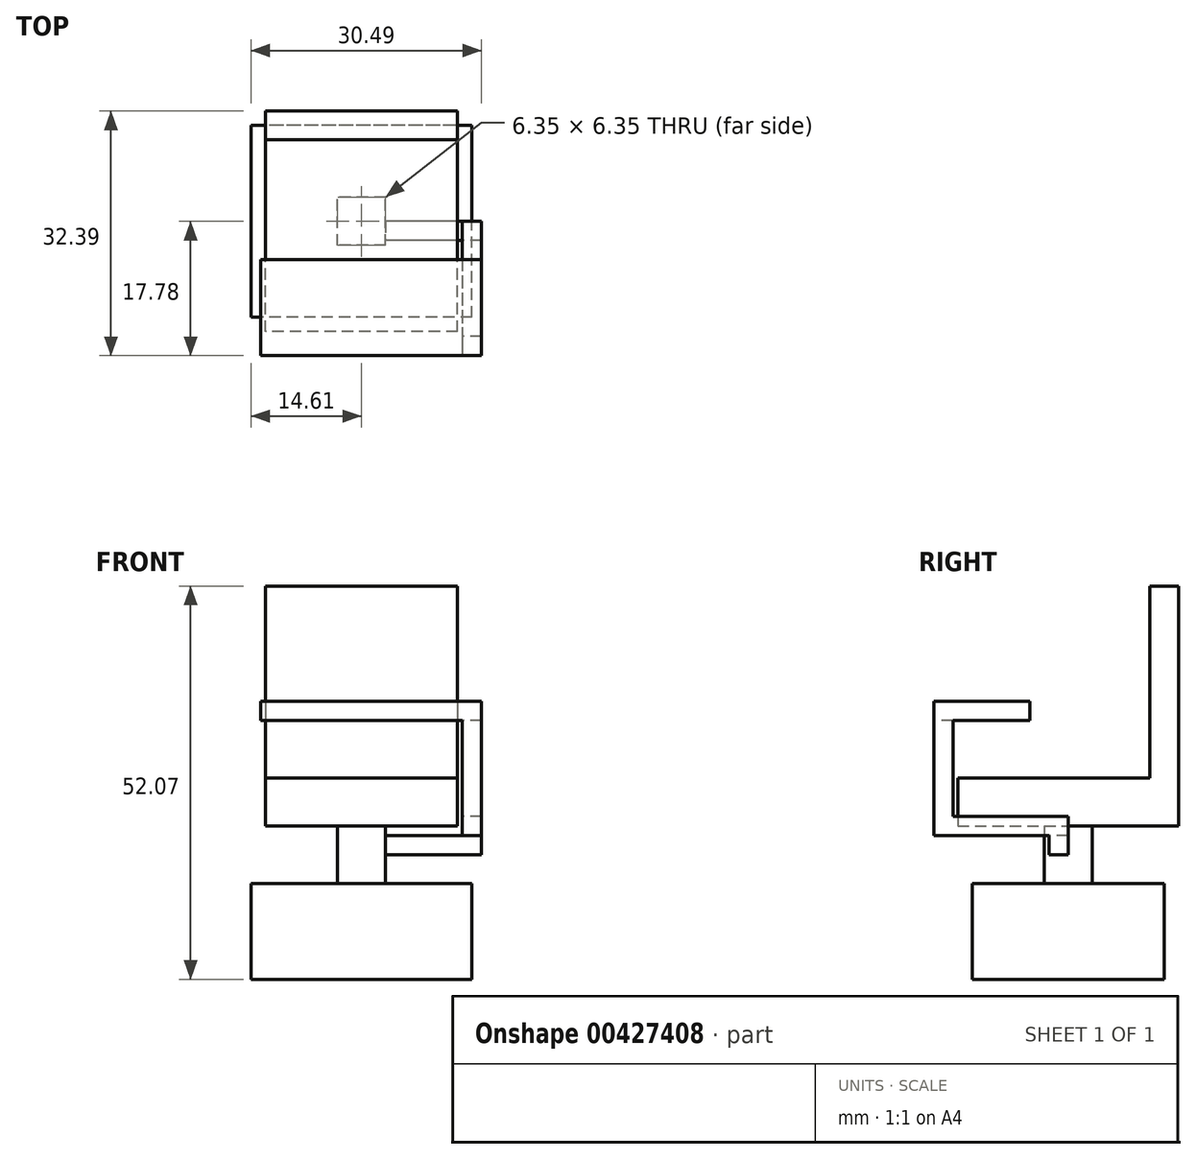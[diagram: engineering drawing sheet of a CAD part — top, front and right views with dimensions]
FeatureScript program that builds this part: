
annotation { "Feature Type Name" : "Feature", "Feature Type Description" : "" }
export const myFeature = defineFeature(function(context is Context, id is Id, definition is map)
    precondition{}
    {
        {
            var Q0;
            Q0=qCreatedBy(makeId("Top.planeOp"),FACE);
            var sketch = newSketch(context, id + "F0", { "sketchPlane" : qUnion([Q0])});
            skLineSegment(sketch, "E0.bottom", {"start": v(14.6, -12.7) * mm, "end": v(-14.6, -12.7) * mm});
            skLineSegment(sketch, "E0.top", {"start": v(14.6, 12.7) * mm, "end": v(-14.6, 12.7) * mm});
            skLineSegment(sketch, "E0.left", {"start": v(14.6, -12.7) * mm, "end": v(14.6, 12.7) * mm});
            skLineSegment(sketch, "E0.right", {"start": v(-14.6, -12.7) * mm, "end": v(-14.6, 12.7) * mm});
            skPoint(sketch, "E0.middle", {"position": v(0, 0) * mm});
            skSolve(sketch);
        }
        {
            var Q0;
            Q0 = qSketchRegion(id + "F0", true);
            extrude(context, id + "F1", {"entities" : qUnion([Q0]), "depth" : 12.7 * mm});
        }
        {
            var Q0;
            Q0=makeQuery(id+"F1.opExtrude","CAP_FACE",FACE,{"disambiguationData":[OSD([sQuery(id+"F0.wireOp",EDGE,"E0.bottom"),sQuery(id+"F0.wireOp",EDGE,"E0.top"),sQuery(id+"F0.wireOp",EDGE,"E0.left"),sQuery(id+"F0.wireOp",EDGE,"E0.right")])],"isStart":false});
            var sketch = newSketch(context, id + "F2", { "sketchPlane" : qUnion([Q0])});
            skLineSegment(sketch, "E1.bottom", {"start": v(3.18, -3.18) * mm, "end": v(-3.18, -3.18) * mm});
            skLineSegment(sketch, "E1.top", {"start": v(3.18, 3.18) * mm, "end": v(-3.18, 3.18) * mm});
            skLineSegment(sketch, "E1.left", {"start": v(3.18, -3.18) * mm, "end": v(3.18, 3.17) * mm});
            skLineSegment(sketch, "E1.right", {"start": v(-3.18, -3.18) * mm, "end": v(-3.18, 3.17) * mm});
            skPoint(sketch, "E1.middle", {"position": v(0, 0) * mm});
            skSolve(sketch);
        }
        {
            var Q0;
            Q0 = qSketchRegion(id + "F2", true);
            extrude(context, id + "F3", {"entities" : qUnion([Q0]), "operationType" : NewBodyOperationType.ADD, "depth" : 7.62 * mm});
        }
        {
            var Q0;
            Q0=makeQuery(id+"F3.opExtrude","CAP_FACE",FACE,{"disambiguationData":[OSD([sQuery(id+"F2.wireOp",EDGE,"E1.bottom"),sQuery(id+"F2.wireOp",EDGE,"E1.top"),sQuery(id+"F2.wireOp",EDGE,"E1.left"),sQuery(id+"F2.wireOp",EDGE,"E1.right")])],"isStart":false});
            var sketch = newSketch(context, id + "F4", { "sketchPlane" : qUnion([Q0])});
            skLineSegment(sketch, "E2.bottom", {"start": v(12.7, -14.6) * mm, "end": v(-12.7, -14.6) * mm});
            skLineSegment(sketch, "E2.top", {"start": v(12.7, 14.6) * mm, "end": v(-12.7, 14.6) * mm});
            skLineSegment(sketch, "E2.left", {"start": v(12.7, -14.6) * mm, "end": v(12.7, 14.6) * mm});
            skLineSegment(sketch, "E2.right", {"start": v(-12.7, -14.6) * mm, "end": v(-12.7, 14.6) * mm});
            skPoint(sketch, "E2.middle", {"position": v(0, 0) * mm});
            skPoint(sketch, "E3.middle", {"position": v(11.23, -12.7) * mm});
            skSolve(sketch);
        }
        {
            var Q0;
            Q0 = qSketchRegion(id + "F4", true);
            extrude(context, id + "F5", {"entities" : qUnion([Q0]), "operationType" : NewBodyOperationType.ADD, "depth" : 6.35 * mm});
        }
        {
            var Q0;
            Q0=makeQuery(id+"F5.opExtrude","CAP_FACE",FACE,{"disambiguationData":[OSD([sQuery(id+"F4.wireOp",EDGE,"E2.bottom"),sQuery(id+"F4.wireOp",EDGE,"E2.top"),sQuery(id+"F4.wireOp",EDGE,"E2.left"),sQuery(id+"F4.wireOp",EDGE,"E2.right")])],"isStart":false});
            var sketch = newSketch(context, id + "F6", { "sketchPlane" : qUnion([Q0])});
            skLineSegment(sketch, "E4.bottom", {"start": v(-12.7, 14.6) * mm, "end": v(12.7, 14.6) * mm});
            skLineSegment(sketch, "E4.top", {"start": v(-12.7, 10.8) * mm, "end": v(12.7, 10.8) * mm});
            skLineSegment(sketch, "E4.left", {"start": v(-12.7, 14.6) * mm, "end": v(-12.7, 10.8) * mm});
            skLineSegment(sketch, "E4.right", {"start": v(12.7, 14.6) * mm, "end": v(12.7, 10.8) * mm});
            skSolve(sketch);
        }
        {
            var Q0;
            Q0 = qSketchRegion(id + "F6", true);
            extrude(context, id + "F7", {"entities" : qUnion([Q0]), "operationType" : NewBodyOperationType.ADD, "depth" : 25.4 * mm});
        }
        {
            var Q0;
            Q0=makeQuery(id+"F3.opExtrude","SWEPT_FACE",FACE,{"disambiguationData":[OSD([sQuery(id+"F2.wireOp",EDGE,"E1.left")])]});
            var sketch = newSketch(context, id + "F8", { "sketchPlane" : qUnion([Q0])});
            skLineSegment(sketch, "E5", {"start": v(0, 20.32) * mm, "end": v(0, 12.7) * mm});
            skLineSegment(sketch, "E6", {"start": v(0, 12.7) * mm, "end": v(0, 16.51) * mm});
            skPoint(sketch, "E7.middle", {"position": v(0, 16.51) * mm});
            skLineSegment(sketch, "E8.bottom", {"start": v(0, 16.51) * mm, "end": v(-2.54, 16.51) * mm});
            skLineSegment(sketch, "E8.top", {"start": v(0, 19.05) * mm, "end": v(-2.54, 19.05) * mm});
            skLineSegment(sketch, "E8.left", {"start": v(0, 16.51) * mm, "end": v(0, 19.05) * mm});
            skLineSegment(sketch, "E8.right", {"start": v(-2.54, 16.51) * mm, "end": v(-2.54, 19.05) * mm});
            skSolve(sketch);
        }
        {
            var Q0;
            Q0 = qSketchRegion(id + "F8", true);
            extrude(context, id + "F9", {"entities" : qUnion([Q0]), "operationType" : NewBodyOperationType.ADD, "depth" : 12.7 * mm});
        }
        {
            var Q0;
            Q0=makeQuery(id+"F9.opExtrude","SWEPT_FACE",FACE,{"disambiguationData":[OSD([sQuery(id+"F8.wireOp",EDGE,"E8.top")])]});
            var sketch = newSketch(context, id + "F10", { "sketchPlane" : qUnion([Q0])});
            skLineSegment(sketch, "E9.bottom", {"start": v(15.88, 0) * mm, "end": v(13.33, 0) * mm});
            skLineSegment(sketch, "E9.top", {"start": v(15.88, -17.78) * mm, "end": v(13.34, -17.78) * mm});
            skLineSegment(sketch, "E9.left", {"start": v(15.88, 0) * mm, "end": v(15.88, -17.78) * mm});
            skLineSegment(sketch, "E9.right", {"start": v(13.33, 0) * mm, "end": v(13.33, -17.78) * mm});
            skSolve(sketch);
        }
        {
            var Q0;
            Q0 = qSketchRegion(id + "F10", true);
            extrude(context, id + "F11", {"entities" : qUnion([Q0]), "operationType" : NewBodyOperationType.ADD, "depth" : 2.54 * mm});
        }
        {
            var Q0;
            Q0=makeQuery(id+"F11.opExtrude","CAP_FACE",FACE,{"disambiguationData":[OSD([sQuery(id+"F10.wireOp",EDGE,"E9.bottom"),sQuery(id+"F10.wireOp",EDGE,"E9.top"),sQuery(id+"F10.wireOp",EDGE,"E9.left"),sQuery(id+"F10.wireOp",EDGE,"E9.right")])],"isStart":false});
            var sketch = newSketch(context, id + "F12", { "sketchPlane" : qUnion([Q0])});
            skLineSegment(sketch, "E10.bottom", {"start": v(15.88, -17.78) * mm, "end": v(13.33, -17.78) * mm});
            skLineSegment(sketch, "E10.top", {"start": v(15.88, -15.24) * mm, "end": v(13.33, -15.24) * mm});
            skLineSegment(sketch, "E10.left", {"start": v(15.88, -17.78) * mm, "end": v(15.88, -15.24) * mm});
            skLineSegment(sketch, "E10.right", {"start": v(13.33, -17.78) * mm, "end": v(13.33, -15.24) * mm});
            skSolve(sketch);
        }
        {
            var Q0;
            Q0 = qSketchRegion(id + "F12", true);
            extrude(context, id + "F13", {"entities" : qUnion([Q0]), "operationType" : NewBodyOperationType.ADD, "depth" : 12.7 * mm});
        }
        {
            var Q0;
            Q0=makeQuery(id+"F13.opExtrude","CAP_FACE",FACE,{"disambiguationData":[OSD([sQuery(id+"F12.wireOp",EDGE,"E10.bottom"),sQuery(id+"F12.wireOp",EDGE,"E10.top"),sQuery(id+"F12.wireOp",EDGE,"E10.left"),sQuery(id+"F12.wireOp",EDGE,"E10.right")])],"isStart":false});
            var sketch = newSketch(context, id + "F14", { "sketchPlane" : qUnion([Q0])});
            skLineSegment(sketch, "E11.bottom", {"start": v(15.87, -17.78) * mm, "end": v(-13.33, -17.78) * mm});
            skLineSegment(sketch, "E11.top", {"start": v(15.87, -5.08) * mm, "end": v(-13.33, -5.08) * mm});
            skLineSegment(sketch, "E11.left", {"start": v(15.88, -17.78) * mm, "end": v(15.88, -5.08) * mm});
            skLineSegment(sketch, "E11.right", {"start": v(-13.33, -17.78) * mm, "end": v(-13.33, -5.08) * mm});
            skSolve(sketch);
        }
        {
            var Q0;
            Q0 = qSketchRegion(id + "F14", true);
            extrude(context, id + "F15", {"entities" : qUnion([Q0]), "operationType" : NewBodyOperationType.ADD, "depth" : 2.54 * mm});
        }
    });
